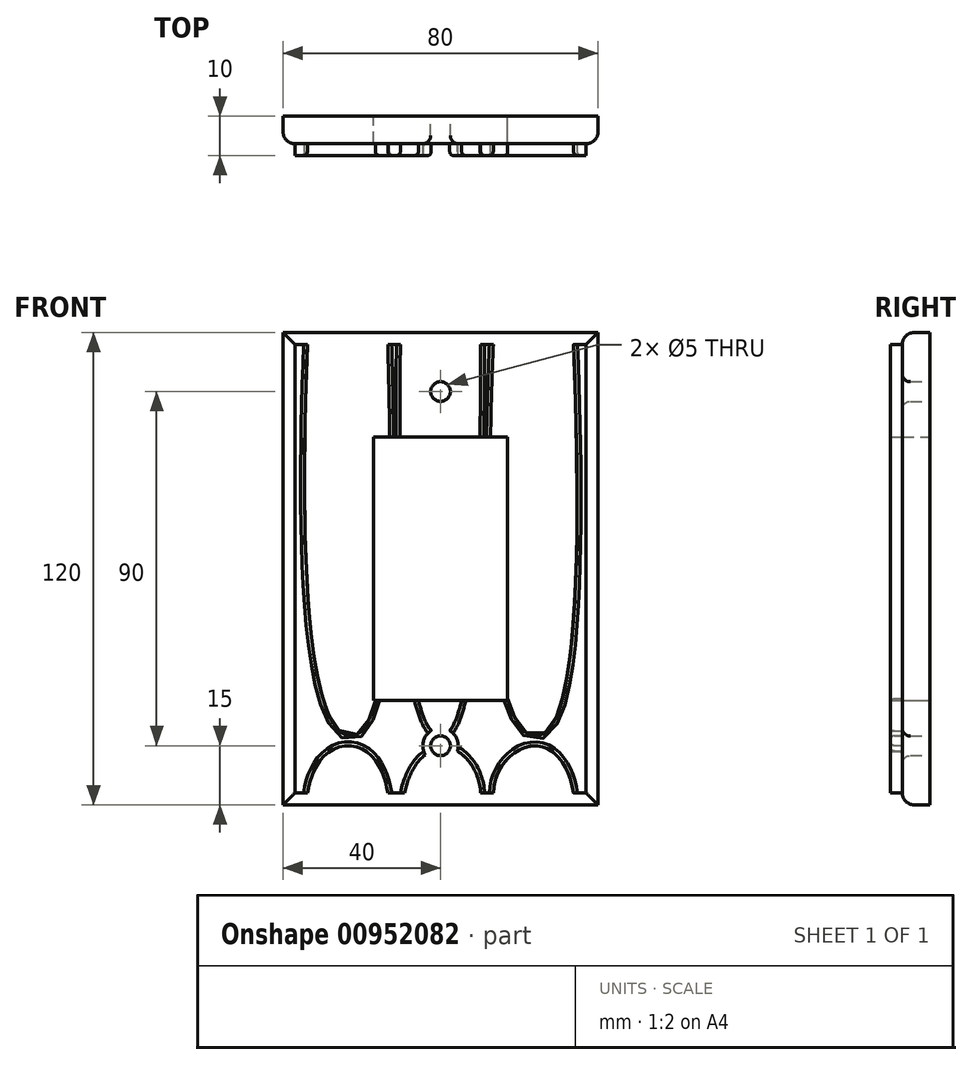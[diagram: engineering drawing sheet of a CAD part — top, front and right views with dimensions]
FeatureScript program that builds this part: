
annotation { "Feature Type Name" : "Feature", "Feature Type Description" : "" }
export const myFeature = defineFeature(function(context is Context, id is Id, definition is map)
    precondition{}
    {
        {
            var Q0;
            Q0=qCreatedBy(makeId("Front.planeOp"),FACE);
            var sketch = newSketch(context, id + "F0", { "sketchPlane" : qUnion([Q0])});
            skLineSegment(sketch, "E0.bottom", {"start": v(-40, 60) * mm, "end": v(40, 60) * mm});
            skLineSegment(sketch, "E0.top", {"start": v(-40, -60) * mm, "end": v(40, -60) * mm});
            skLineSegment(sketch, "E0.left", {"start": v(-40, 60) * mm, "end": v(-40, -60) * mm});
            skLineSegment(sketch, "E0.right", {"start": v(40, 60) * mm, "end": v(40, -60) * mm});
            skPoint(sketch, "E0.middle", {"position": v(0, 0) * mm});
            skLineSegment(sketch, "E1.bottom", {"start": v(-17, 33.5) * mm, "end": v(17, 33.5) * mm});
            skLineSegment(sketch, "E1.top", {"start": v(-17, -33.5) * mm, "end": v(17, -33.5) * mm});
            skLineSegment(sketch, "E1.left", {"start": v(-17, 33.5) * mm, "end": v(-17, -33.5) * mm});
            skLineSegment(sketch, "E1.right", {"start": v(17, 33.5) * mm, "end": v(17, -33.5) * mm});
            skLineSegment(sketch, "E2", {"start": v(0, 60) * mm, "end": v(0, 45) * mm, "construction": true});
            skLineSegment(sketch, "E3", {"start": v(0, -60) * mm, "end": v(0, -45) * mm, "construction": true});
            skCircle(sketch, "E4", {"center": v(0, 45) * mm, "radius": 3.5 * mm});
            skCircle(sketch, "E5", {"center": v(0, -45) * mm, "radius": 3.5 * mm});
            skCircle(sketch, "E6", {"center": v(0, -45) * mm, "radius": 2.5 * mm});
            skCircle(sketch, "E7", {"center": v(0, 45) * mm, "radius": 2.5 * mm});
            skSolve(sketch);
        }
        {
            var Q0;
            Q0=makeQuery(id+"F0.imprint","IMPRINT",FACE,{"disambiguationData":[TD([[makeQuery(id+"F0.imprint","IMPRINT",EDGE,{"derivedFrom":sQuery(id+"F0.wireOp",EDGE,"E0.bottom")}),-1.0]])]});
            var Q1;
            Q1=makeQuery(id+"F0.imprint","IMPRINT",FACE,{"disambiguationData":[TD([[makeQuery(id+"F0.imprint","IMPRINT",EDGE,{"derivedFrom":sQuery(id+"F0.wireOp",EDGE,"E4")}),1.0]])]});
            var Q2;
            Q2=makeQuery(id+"F0.imprint","IMPRINT",FACE,{"disambiguationData":[TD([[makeQuery(id+"F0.imprint","IMPRINT",EDGE,{"derivedFrom":sQuery(id+"F0.wireOp",EDGE,"E5")}),1.0]])]});
            extrude(context, id + "F1", {"entities" : qUnion([Q0, Q1, Q2]), "depth" : 7 * mm, "offsetDistance" : 25 * mm});
        }
        {
            var Q0;
            Q0=makeQuery(id+"F1.opExtrude","CAP_EDGE",EDGE,{"disambiguationData":[OSD([sQuery(id+"F0.wireOp",EDGE,"E6")])],"isStart":false});
            var Q1;
            Q1=makeQuery(id+"F1.opExtrude","CAP_EDGE",EDGE,{"disambiguationData":[OSD([sQuery(id+"F0.wireOp",EDGE,"E7")])],"isStart":false});
            fillet(context, id + "F2", {"entities" : qUnion([Q0, Q1]), "radius" : 2 * mm, "tangentPropagation" : true, "allowEdgeOverflow" : false});
        }
        {
            var Q0;
            Q0=makeQuery(id+"F1.opExtrude","CAP_EDGE",EDGE,{"disambiguationData":[OSD([sQuery(id+"F0.wireOp",EDGE,"E0.right")])],"isStart":false});
            var Q1;
            Q1=makeQuery(id+"F1.opExtrude","CAP_EDGE",EDGE,{"disambiguationData":[OSD([sQuery(id+"F0.wireOp",EDGE,"E0.bottom")])],"isStart":false});
            var Q2;
            Q2=makeQuery(id+"F1.opExtrude","CAP_EDGE",EDGE,{"disambiguationData":[OSD([sQuery(id+"F0.wireOp",EDGE,"E0.left")])],"isStart":false});
            var Q3;
            Q3=makeQuery(id+"F1.opExtrude","CAP_EDGE",EDGE,{"disambiguationData":[OSD([sQuery(id+"F0.wireOp",EDGE,"E0.top")])],"isStart":false});
            fillet(context, id + "F3", {"entities" : qUnion([Q0, Q1, Q2, Q3]), "radius" : 3 * mm, "tangentPropagation" : true, "allowEdgeOverflow" : false});
        }
        {
            var Q0;
            Q0=makeQuery(id+"F1.opExtrude","CAP_FACE",FACE,{"disambiguationData":[OSD([sQuery(id+"F0.wireOp",EDGE,"E0.bottom"),sQuery(id+"F0.wireOp",EDGE,"E0.top"),sQuery(id+"F0.wireOp",EDGE,"E0.left"),sQuery(id+"F0.wireOp",EDGE,"E0.right"),sQuery(id+"F0.wireOp",EDGE,"E1.bottom"),sQuery(id+"F0.wireOp",EDGE,"E1.top"),sQuery(id+"F0.wireOp",EDGE,"E1.left"),sQuery(id+"F0.wireOp",EDGE,"E1.right"),sQuery(id+"F0.wireOp",EDGE,"E6"),sQuery(id+"F0.wireOp",EDGE,"E7")])],"isStart":false});
            var sketch = newSketch(context, id + "F4", { "sketchPlane" : qUnion([Q0])});
            skFitSpline(sketch, "E8", {"points": [v(-10.2, 57) * mm, v(0, -42.47) * mm, v(10.2, 57) * mm], "startDerivative": vector(-5.42, -495) * mm, "endDerivative": vector(0.73, 495) * mm});
            skFitSpline(sketch, "E9", {"points": [v(33.8, 57) * mm, v(24.2, -42.47) * mm, v(13.4, 57) * mm], "startDerivative": vector(19.2, -495.15) * mm, "endDerivative": vector(19.92, 494.84) * mm});
            skFitSpline(sketch, "E10", {"points": [v(-33.8, 57) * mm, v(-22.8, -42.47) * mm, v(-13.4, 57) * mm], "startDerivative": vector(-19.2, -494.8) * mm, "endDerivative": vector(-13.79, 495.2) * mm});
            skLineSegment(sketch, "E11", {"start": v(-37, 57) * mm, "end": v(37, 57) * mm, "construction": true});
            skFitSpline(sketch, "E12", {"points": [v(-10.2, -57) * mm, v(0, -45) * mm, v(10.2, -57) * mm], "startDerivative": vector(9.68, 45.4) * mm, "endDerivative": vector(2.36, -43.2) * mm});
            skFitSpline(sketch, "E13", {"points": [v(-33.8, -57) * mm, v(-22.8, -45) * mm, v(-13.4, -57) * mm], "startDerivative": vector(8.42, 52.31) * mm, "endDerivative": vector(6.84, -46.13) * mm});
            skFitSpline(sketch, "E14", {"points": [v(13.4, -57) * mm, v(24.2, -45) * mm, v(33.8, -57) * mm], "startDerivative": vector(1.42, 43.1) * mm, "endDerivative": vector(6.45, -42.63) * mm});
            skSolve(sketch);
        }
        {
            var Q0;
            {var subQ19=sQuery(id+"F4.wireOp",EDGE,"E14");Q0=makeQuery(id+"F4.imprint","IMPRINT",FACE,{"disambiguationData":[TD([[makeQuery(id+"F4.imprint","IMPRINT",EDGE,{"derivedFrom":subQ19}),1.0]])]});}
            var Q1;
            {var subQ0=sQuery(id+"F4.wireOp",EDGE,"E13");Q1=makeQuery(id+"F4.imprint","IMPRINT",FACE,{"disambiguationData":[TD([[makeQuery(id+"F4.imprint","IMPRINT",EDGE,{"derivedFrom":subQ0}),1.0]])]});}
            var Q2;
            {var subQ0=sQuery(id+"F4.wireOp",EDGE,"E8");var subQ1=sQuery(id+"F0.wireOp",EDGE,"E1.bottom");var subQ5=makeQuery(id+"F1.opExtrude","CAP_EDGE",EDGE,{"disambiguationData":[OSD([subQ1])],"isStart":false});var subQ6=makeQuery(id+"F4.imprint","INTERSECT",VERTEX,{"disambiguationData":[OD(1.0)],"derivedFrom":[subQ5,subQ0]});Q2=makeQuery(id+"F4.imprint","IMPRINT",FACE,{"disambiguationData":[TD([[makeQuery(id+"F4.imprint","IMPRINT",EDGE,{"disambiguationData":[TD([[subQ6,-1.0]])],"derivedFrom":subQ5}),1.0]])]});}
            var Q3;
            {var subQ0=sQuery(id+"F4.wireOp",EDGE,"E8");var subQ1=sQuery(id+"F0.wireOp",EDGE,"E1.bottom");var subQ5=makeQuery(id+"F1.opExtrude","CAP_EDGE",EDGE,{"disambiguationData":[OSD([subQ1])],"isStart":false});var subQ6=makeQuery(id+"F4.imprint","INTERSECT",VERTEX,{"disambiguationData":[OD(0.0)],"derivedFrom":[subQ5,subQ0]});Q3=makeQuery(id+"F4.imprint","IMPRINT",FACE,{"disambiguationData":[TD([[makeQuery(id+"F4.imprint","IMPRINT",EDGE,{"disambiguationData":[TD([[subQ6,1.0]])],"derivedFrom":subQ5}),1.0]])]});}
            extrude(context, id + "F5", {"entities" : qUnion([Q0, Q1, Q2, Q3]), "operationType" : NewBodyOperationType.ADD, "depth" : 3 * mm, "offsetDistance" : 25 * mm});
        }
        {
            var Q0;
            Q0=makeQuery(id+"F5.opExtrude","CAP_EDGE",EDGE,{"disambiguationData":[OSD([sQuery(id+"F4.wireOp",EDGE,"E14")])],"isStart":false});
            var Q1;
            {var subQ0=sQuery(id+"F4.wireOp",EDGE,"E12");var subQ1=sQuery(id+"F0.wireOp",EDGE,"E6");var subQ2=sQuery(id+"F0.wireOp",EDGE,"E0.top");var subQ3=makeQuery(id+"F1.opExtrude","CAP_FACE",FACE,{"disambiguationData":[OSD([sQuery(id+"F0.wireOp",EDGE,"E0.bottom"),subQ2,sQuery(id+"F0.wireOp",EDGE,"E0.left"),sQuery(id+"F0.wireOp",EDGE,"E0.right"),sQuery(id+"F0.wireOp",EDGE,"E1.bottom"),sQuery(id+"F0.wireOp",EDGE,"E1.top"),sQuery(id+"F0.wireOp",EDGE,"E1.left"),sQuery(id+"F0.wireOp",EDGE,"E1.right"),subQ1,sQuery(id+"F0.wireOp",EDGE,"E7")])],"isStart":false});Q1=makeQuery(id+"F5.opExtrude","CAP_EDGE",EDGE,{"disambiguationData":[OSD([subQ0]),TDD([makeQuery(id+"F4.imprint","IMPRINT",EDGE,{"disambiguationData":[TD([[makeQuery(id+"F4.imprint","INTERSECT",VERTEX,{"disambiguationData":[OD(1.0)],"derivedFrom":[makeQuery(id+"F3.opFillet","BLEND_EDGE",EDGE,{"blendedFrom":[makeQuery(id+"F1.opExtrude","CAP_EDGE",EDGE,{"disambiguationData":[OSD([subQ2])],"isStart":false}),subQ3],"blendedInto":[subQ3]}),subQ0]}),1.0]])],"derivedFrom":subQ0})])],"isStart":false});}
            var Q2;
            {var subQ0=sQuery(id+"F4.wireOp",EDGE,"E12");var subQ1=sQuery(id+"F0.wireOp",EDGE,"E6");var subQ2=sQuery(id+"F0.wireOp",EDGE,"E0.top");var subQ3=makeQuery(id+"F1.opExtrude","CAP_FACE",FACE,{"disambiguationData":[OSD([sQuery(id+"F0.wireOp",EDGE,"E0.bottom"),subQ2,sQuery(id+"F0.wireOp",EDGE,"E0.left"),sQuery(id+"F0.wireOp",EDGE,"E0.right"),sQuery(id+"F0.wireOp",EDGE,"E1.bottom"),sQuery(id+"F0.wireOp",EDGE,"E1.top"),sQuery(id+"F0.wireOp",EDGE,"E1.left"),sQuery(id+"F0.wireOp",EDGE,"E1.right"),subQ1,sQuery(id+"F0.wireOp",EDGE,"E7")])],"isStart":false});Q2=makeQuery(id+"F5.opExtrude","CAP_EDGE",EDGE,{"disambiguationData":[OSD([subQ0]),TDD([makeQuery(id+"F4.imprint","IMPRINT",EDGE,{"disambiguationData":[TD([[makeQuery(id+"F4.imprint","INTERSECT",VERTEX,{"disambiguationData":[OD(0.0)],"derivedFrom":[makeQuery(id+"F3.opFillet","BLEND_EDGE",EDGE,{"blendedFrom":[makeQuery(id+"F1.opExtrude","CAP_EDGE",EDGE,{"disambiguationData":[OSD([subQ2])],"isStart":false}),subQ3],"blendedInto":[subQ3]}),subQ0]}),-1.0]])],"derivedFrom":subQ0})])],"isStart":true});}
            var Q3;
            Q3=makeQuery(id+"F5.opExtrude","CAP_EDGE",EDGE,{"disambiguationData":[OSD([sQuery(id+"F4.wireOp",EDGE,"E13")])],"isStart":false});
            var Q4;
            {var subQ0=sQuery(id+"F4.wireOp",EDGE,"E10");var subQ1=sQuery(id+"F0.wireOp",EDGE,"E1.top");Q4=makeQuery(id+"F5.opExtrude","CAP_EDGE",EDGE,{"disambiguationData":[OSD([subQ0]),TDD([makeQuery(id+"F4.imprint","IMPRINT",EDGE,{"disambiguationData":[TD([[makeQuery(id+"F4.imprint","INTERSECT",VERTEX,{"derivedFrom":[makeQuery(id+"F1.opExtrude","CAP_EDGE",EDGE,{"disambiguationData":[OSD([subQ1])],"isStart":false}),subQ0]}),1.0]])],"derivedFrom":subQ0})])],"isStart":false});}
            var Q5;
            {var subQ0=sQuery(id+"F4.wireOp",EDGE,"E8");var subQ2=sQuery(id+"F0.wireOp",EDGE,"E1.top");Q5=makeQuery(id+"F5.opExtrude","CAP_EDGE",EDGE,{"disambiguationData":[OSD([subQ0]),TDD([makeQuery(id+"F4.imprint","IMPRINT",EDGE,{"disambiguationData":[TD([[makeQuery(id+"F4.imprint","INTERSECT",VERTEX,{"disambiguationData":[OD(1.0)],"derivedFrom":[makeQuery(id+"F1.opExtrude","CAP_EDGE",EDGE,{"disambiguationData":[OSD([subQ2])],"isStart":false}),subQ0]}),1.0]])],"derivedFrom":subQ0})])],"isStart":false});}
            var Q6;
            {var subQ0=sQuery(id+"F4.wireOp",EDGE,"E8");var subQ1=sQuery(id+"F0.wireOp",EDGE,"E1.top");Q6=makeQuery(id+"F5.opExtrude","CAP_EDGE",EDGE,{"disambiguationData":[OSD([subQ0]),TDD([makeQuery(id+"F4.imprint","IMPRINT",EDGE,{"disambiguationData":[TD([[makeQuery(id+"F4.imprint","INTERSECT",VERTEX,{"disambiguationData":[OD(0.0)],"derivedFrom":[makeQuery(id+"F1.opExtrude","CAP_EDGE",EDGE,{"disambiguationData":[OSD([subQ1])],"isStart":false}),subQ0]}),-1.0]])],"derivedFrom":subQ0})])],"isStart":false});}
            var Q7;
            {var subQ0=sQuery(id+"F4.wireOp",EDGE,"E9");var subQ1=sQuery(id+"F0.wireOp",EDGE,"E1.right");Q7=makeQuery(id+"F5.opExtrude","CAP_EDGE",EDGE,{"disambiguationData":[OSD([subQ0]),TDD([makeQuery(id+"F4.imprint","IMPRINT",EDGE,{"disambiguationData":[TD([[makeQuery(id+"F4.imprint","INTERSECT",VERTEX,{"derivedFrom":[makeQuery(id+"F1.opExtrude","CAP_EDGE",EDGE,{"disambiguationData":[OSD([subQ1])],"isStart":false}),subQ0]}),1.0]])],"derivedFrom":subQ0})])],"isStart":false});}
            var Q8;
            {var subQ0=sQuery(id+"F4.wireOp",EDGE,"E9");var subQ1=sQuery(id+"F0.wireOp",EDGE,"E1.bottom");Q8=makeQuery(id+"F5.opExtrude","CAP_EDGE",EDGE,{"disambiguationData":[OSD([subQ0]),TDD([makeQuery(id+"F4.imprint","IMPRINT",EDGE,{"disambiguationData":[TD([[makeQuery(id+"F4.imprint","INTERSECT",VERTEX,{"derivedFrom":[makeQuery(id+"F1.opExtrude","CAP_EDGE",EDGE,{"disambiguationData":[OSD([subQ1])],"isStart":false}),subQ0]}),-1.0]])],"derivedFrom":subQ0})])],"isStart":false});}
            var Q9;
            {var subQ0=sQuery(id+"F4.wireOp",EDGE,"E8");var subQ1=sQuery(id+"F0.wireOp",EDGE,"E1.bottom");Q9=makeQuery(id+"F5.opExtrude","CAP_EDGE",EDGE,{"disambiguationData":[OSD([subQ0]),TDD([makeQuery(id+"F4.imprint","IMPRINT",EDGE,{"disambiguationData":[TD([[makeQuery(id+"F4.imprint","INTERSECT",VERTEX,{"disambiguationData":[OD(1.0)],"derivedFrom":[makeQuery(id+"F1.opExtrude","CAP_EDGE",EDGE,{"disambiguationData":[OSD([subQ1])],"isStart":false}),subQ0]}),-1.0]])],"derivedFrom":subQ0})])],"isStart":false});}
            var Q10;
            {var subQ0=sQuery(id+"F4.wireOp",EDGE,"E8");var subQ1=sQuery(id+"F0.wireOp",EDGE,"E1.bottom");Q10=makeQuery(id+"F5.opExtrude","CAP_EDGE",EDGE,{"disambiguationData":[OSD([subQ0]),TDD([makeQuery(id+"F4.imprint","IMPRINT",EDGE,{"disambiguationData":[TD([[makeQuery(id+"F4.imprint","INTERSECT",VERTEX,{"disambiguationData":[OD(0.0)],"derivedFrom":[makeQuery(id+"F1.opExtrude","CAP_EDGE",EDGE,{"disambiguationData":[OSD([subQ1])],"isStart":false}),subQ0]}),1.0]])],"derivedFrom":subQ0})])],"isStart":false});}
            var Q11;
            {var subQ0=sQuery(id+"F4.wireOp",EDGE,"E10");var subQ1=sQuery(id+"F0.wireOp",EDGE,"E1.bottom");Q11=makeQuery(id+"F5.opExtrude","CAP_EDGE",EDGE,{"disambiguationData":[OSD([subQ0]),TDD([makeQuery(id+"F4.imprint","IMPRINT",EDGE,{"disambiguationData":[TD([[makeQuery(id+"F4.imprint","INTERSECT",VERTEX,{"derivedFrom":[makeQuery(id+"F1.opExtrude","CAP_EDGE",EDGE,{"disambiguationData":[OSD([subQ1])],"isStart":false}),subQ0]}),-1.0]])],"derivedFrom":subQ0})])],"isStart":false});}
            fillet(context, id + "F6", {"entities" : qUnion([Q0, Q1, Q2, Q3, Q4, Q5, Q6, Q7, Q8, Q9, Q10, Q11]), "radius" : 1 * mm, "tangentPropagation" : true, "allowEdgeOverflow" : false});
        }
    });
